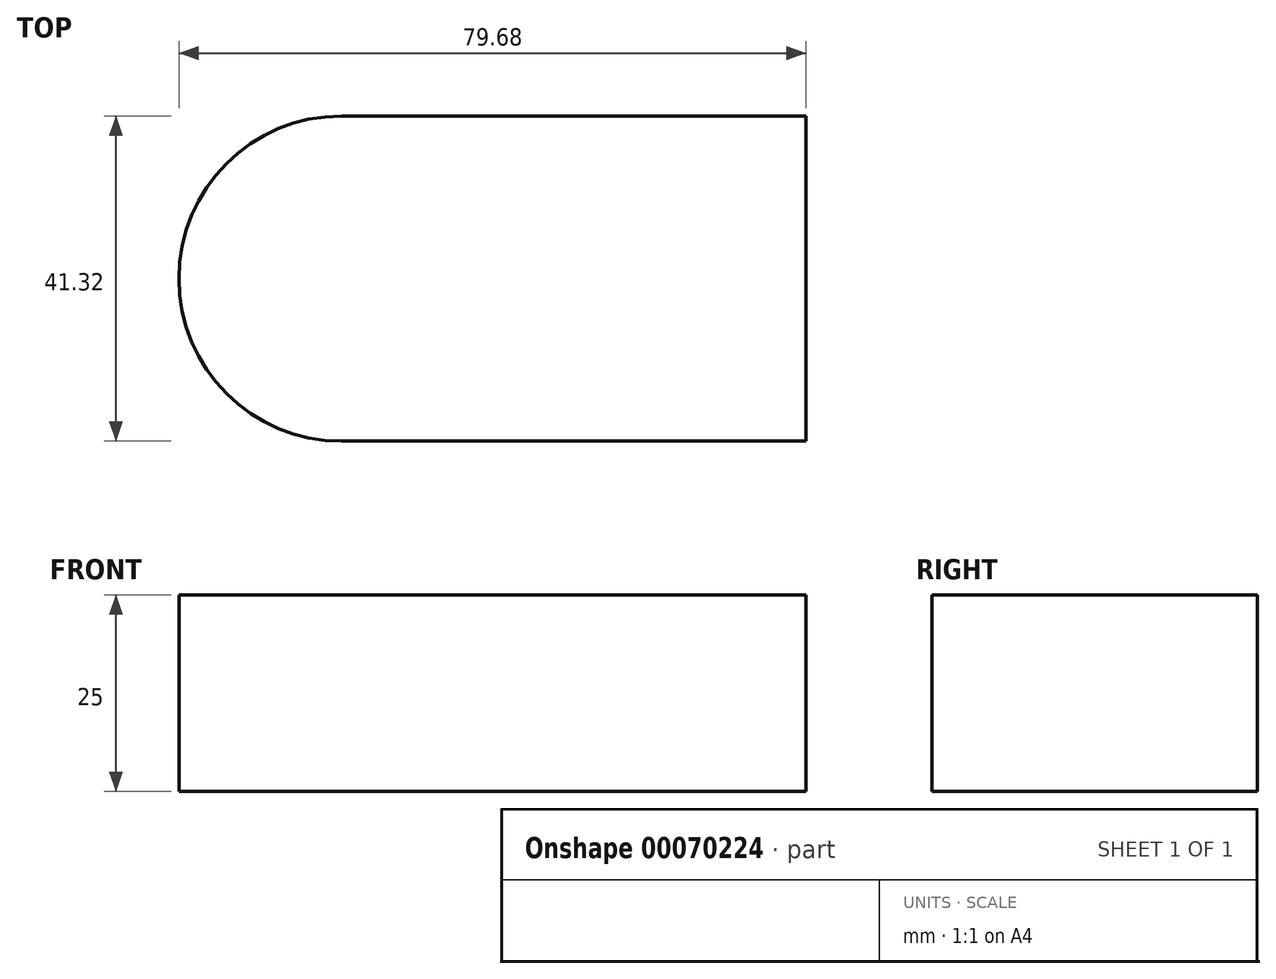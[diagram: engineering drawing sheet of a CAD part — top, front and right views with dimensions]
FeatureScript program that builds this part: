
annotation { "Feature Type Name" : "Feature", "Feature Type Description" : "" }
export const myFeature = defineFeature(function(context is Context, id is Id, definition is map)
    precondition{}
    {
        {
            var Q0;
            Q0=qCreatedBy(makeId("Top.planeOp"),FACE);
            var sketch = newSketch(context, id + "F0", { "sketchPlane" : qUnion([Q0])});
            skLineSegment(sketch, "E0.rect.bottom", {"start": v(29.5, 20.66) * mm, "end": v(-29.5, 20.66) * mm});
            skLineSegment(sketch, "E0.rect.top", {"start": v(29.5, -20.66) * mm, "end": v(-29.5, -20.66) * mm});
            skLineSegment(sketch, "E0.rect.left", {"start": v(29.5, 20.66) * mm, "end": v(29.5, -20.66) * mm});
            skPoint(sketch, "E0.rect.middle", {"position": v(0, 0) * mm});
            skArc(sketch, "E1", {"start": v(-29.5, 20.66) * mm, "mid": v(-50.17, 0) * mm, "end": v(-29.5, -20.66) * mm});
            skSolve(sketch);
        }
        {
            var Q0;
            Q0 = qSketchRegion(id + "F0", true);
            extrude(context, id + "F1", {"entities" : qUnion([Q0]), "depth" : 25 * mm});
        }
    });
